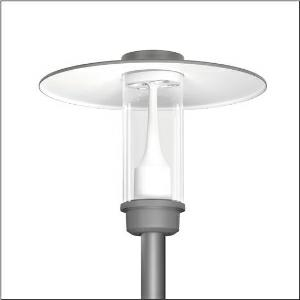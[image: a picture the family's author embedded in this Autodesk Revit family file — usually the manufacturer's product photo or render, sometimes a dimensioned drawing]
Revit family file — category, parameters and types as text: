
# Revit family: litepole_2_iq___p1_0a_5xa5425bf14h_a5ac
name_source: partatom
category: Lighting Fixtures
units: mm (PartAtom-declared; Revit-internal decimal feet)

## family parameters
Cut with Voids When Loaded = No
Host = Face
Light Source = No
Part Type = Normal
Room Calculation Point = No
Round Connector Dimension = Use Diameter
Shared = No

## types (1)
- --- (1 x LED, 1520 lm, 12.9 W, 2200K)
    Apparent Load = 13 VA
    CIE Flux Codes = 33 62 89 96 100
    Color Rendering = 70
    Color Temperature = 2200K
    Default Elevation = 1800 mm
    Description = Litepole 2 iQ, mast luminaire, Module 540 iQ-SR, primary light control with 3 zone facetted reflector, of plastic, silver coated, highly specular, structured, primary optical cover: cover, of PMMA, transparent, light distribution: P1.0a, light emission: direct distribution, primary light characteristic: strongly asymmetric, installation type: post-top, LED, High Power LED, rated luminous flux: 1.520lm, luminous efficacy: 118lm/W, light colour: 722, colour temperature: 2200K, control gear: iQ Street-Remote, control: pre-setting: logarithmic dimming characteristic, Street-Remote, Auto-Match, Temp-Guard, Lumen-Switch, Night-Set, Smart-Wire, Light-Fading, Desk-Remote (wireless, voltage-free reading and setting of iQ features in the workshop via application-optimized NFC function/RFID function), optimised constant luminous flux control (CLO 2.0), with terminal, 6-pole, max. 2.5mm², mains connection: 230..240V, AC, 50/60Hz, start of lifetime: 13W, end of service life: 13W, reduction: 6W, luminaire housing, upper part, of aluminium, coated, Siteco® metallic grey (DB 702S), diameter: 750mm, height: 590mm, spigot size: d x l = 76 x 70mm (post-top) | with reducer (optional accessory) 60 x 70mm, mounting height: 3..5m, post-top mast mounting element, of diecast aluminium, coated, Siteco® metallic grey (DB 702S), Module 540 iQ-SR, traffic white (RAL 9016), equipment: standard, protection rating (complete): IP65, insulation class (complete): insulation class II (safety insulation), certification: CE, ENEC, VDE, packaging unit: 1 piece

Light Distribution: P1.0a
    Height = 590 mm
    Lamp = 1 x LED
    Lamp Light Flux = 1520 lm
    Lamp Power = 12.9 W
    Lamp count = 1
    Length = 750 mm
    Luminous efficacy = 118 lm/W
    Manufacturer = Siteco
    ModVariant = No
    Model = 5XA5425BF14H
    Number of Poles = 1
    OnlyDefault = Yes
    Power Factor = 1
    Product Name = Litepole 2 iQ | P1.0a
    Product group = mast luminaire | pylon top
    ProductGroupID = 6100
    Protection Class = Protection class II
    Protection Degree = IP 65
    RLX_Detail_Level = 1
    RLX_Emergency_Light_Flux = 0 lm
    RLX_Emergency_Type = 0
    RLX_Emergency_Type_DB = No
    RlxData = <blob elided: 55853 chars, md5=95e50727>
    Socket = socket
    Standby Power = 0 W
    System Light Flux = 1520 lm
    System Power = 13 W
    Type Comments = factory setting: luminous flux: 100 % | dim-lin: 254 | 516 mA
    Type Image = l_1006518.jpg
    URL = http://relux.com
    VarID = @adj_190009
    Voltage = 0 V
    Weight = 0.00 kg
    Width = 0 mm  [stored 0 ft]

note: [stored X ft] marks values corroborated as IEEE doubles in the binary element streams (Revit-internal decimal feet)

## geometry (parser evidence)
native form markers: Blend x4, Sweep x9
no freeform markers — native parametric forms only
